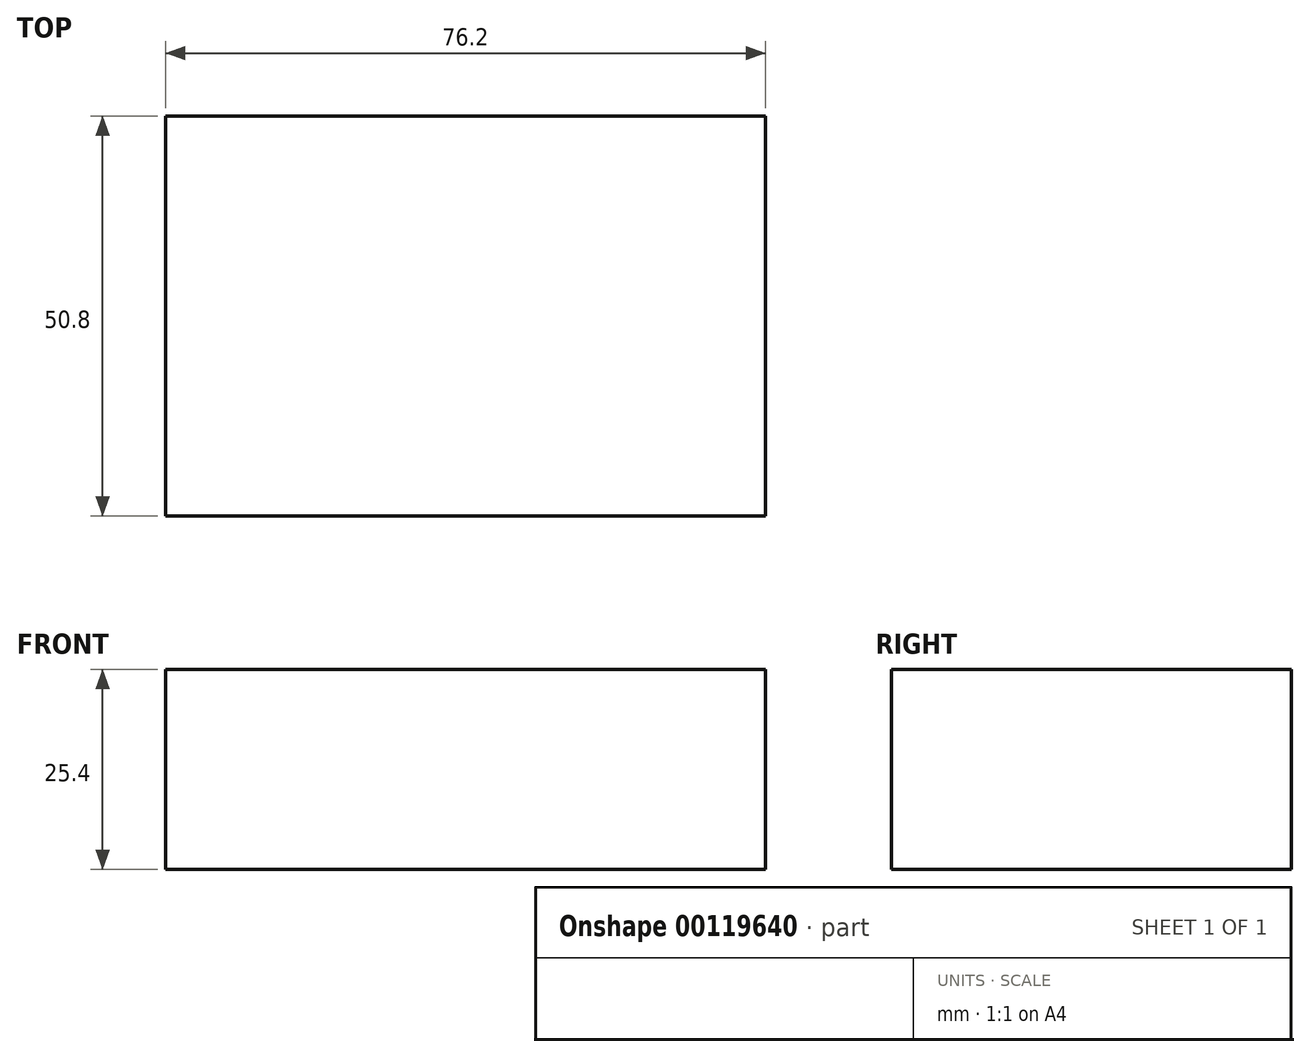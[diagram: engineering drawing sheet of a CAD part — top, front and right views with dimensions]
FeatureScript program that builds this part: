
annotation { "Feature Type Name" : "Feature", "Feature Type Description" : "" }
export const myFeature = defineFeature(function(context is Context, id is Id, definition is map)
    precondition{}
    {
        {
            var Q0;
            Q0=qCreatedBy(makeId("Top.planeOp"),FACE);
            var sketch = newSketch(context, id + "F0", { "sketchPlane" : qUnion([Q0])});
            skLineSegment(sketch, "E0.bottom", {"start": v(38.1, -25.4) * mm, "end": v(-38.1, -25.4) * mm});
            skLineSegment(sketch, "E0.top", {"start": v(38.1, 25.4) * mm, "end": v(-38.1, 25.4) * mm});
            skLineSegment(sketch, "E0.left", {"start": v(38.1, -25.4) * mm, "end": v(38.1, 25.4) * mm});
            skLineSegment(sketch, "E0.right", {"start": v(-38.1, -25.4) * mm, "end": v(-38.1, 25.4) * mm});
            skPoint(sketch, "E0.middle", {"position": v(0, 0) * mm});
            skSolve(sketch);
        }
        {
            var Q0;
            Q0 = qSketchRegion(id + "F0", true);
            extrude(context, id + "F1", {"entities" : qUnion([Q0]), "depth" : 25.4 * mm});
        }
    });
